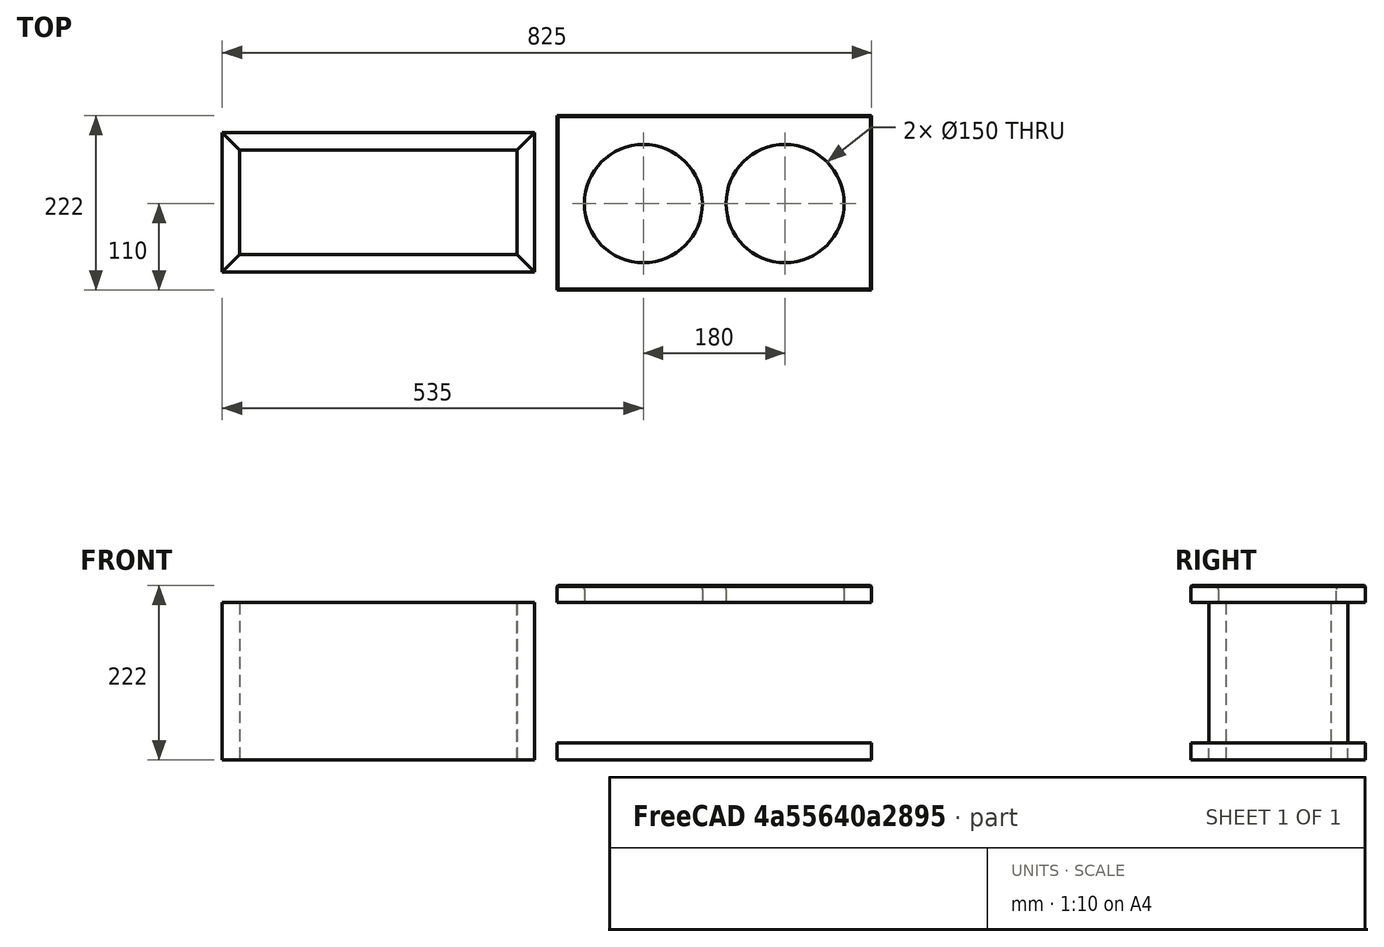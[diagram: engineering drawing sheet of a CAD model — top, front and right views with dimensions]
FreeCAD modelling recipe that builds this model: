
FCSTD DOCUMENT  (FreeCAD 0.16R6706 (Git))
Label: planter
License: All rights reserved
LicenseURL: http://en.wikipedia.org/wiki/All_rights_reserved
objects: Part::Box×14, Part::Cut×10, Part::Extrusion×2, Part::Fillet×2, Part::Part2DObjectPython×1, Part::Chamfer×1
note: 30 computed .brp shape members not serialized (recipe doc carries the construction recipe); baked Part::Feature solids carry a one-line shape summary decoded from their .brp

FEATURE [Part::Box] Box  label="front"
  Height = 200
  Length = 400
  Placement = pos=(-425,23,0) rot=(0,0,1;0rad)
  Width = 22
FEATURE [Part::Box] Box002  label="left"
  Height = 200
  Length = 178
  Placement = pos=(-400,22,0) rot=(0,0,1;1.5708rad)
  Width = 22
FEATURE [Part::Box] Box004  label="base"
  Height = 222
  Length = 400
  Placement = pos=(0,222,0) rot=(1,0,0;1.5708rad)
  Width = 22
FEATURE [Part::Box] Box005  label="top"
  Height = 222
  Length = 400
  Placement = pos=(0,222,200) rot=(1,0,0;1.5708rad)
  Width = 22
FEATURE [Part::Part2DObjectPython] Circle  # Draft 2D object (typed FeaturePython)
  FirstAngle = 0
  LastAngle = 0
  MakeFace = true
  Placement = pos=(110,110,222) rot=(0,0,1;1.5708rad)
  Radius = 75
FEATURE [Part::Extrusion] Extrude
  Base = -> Circle
  Dir = (0,0,22)
  Placement = pos=(0,0,-22) rot=(0,0,1;0rad)
  Solid = true
FEATURE [Part::Extrusion] Extrude001
  Base = -> Circle
  Dir = (0,0,22)
  Placement = pos=(180,0,-22) rot=(0,0,1;0rad)
  Solid = true
FEATURE [Part::Cut] Cut
  Base = -> Box005
  Tool = -> Extrude
FEATURE [Part::Cut] Cut001
  Base = -> Cut
  Tool = -> Extrude001
FEATURE [Part::Fillet] Fillet
  Base = -> Cut001
  Edges = 1 edges r=5: [Edge15]
FEATURE [Part::Chamfer] Chamfer
  Base = -> Fillet
  Edges = 4 edges r=1.5: [Edge2,Edge3,Edge4,Edge5]
FEATURE [Part::Fillet] Fillet001  label="Top"
  Base = -> Chamfer
  Edges = 1 edges r=5: [Edge6]
FEATURE [Part::Box] Box006  label="45degree"
  Height = 300
  Length = 24
  Placement = pos=(-26.4,21,-14) rot=(0,0,1;0.785398rad)
  Width = 36
FEATURE [Part::Box] Box007  label="45degree001"
  Height = 300
  Length = 23
  Placement = pos=(-443.5,37,-31) rot=(0,0,-1;0.785398rad)
  Width = 36
FEATURE [Part::Box] Box008  label="front001"
  Height = 200
  Length = 400
  Placement = pos=(25,0,0) rot=(0,0,1;0rad)
  Width = 22
FEATURE [Part::Box] Box009  label="45degree002"
  Height = 300
  Length = 23
  Placement = pos=(425,0,-16) rot=(0,0,1;0.785398rad)
  Width = 34
FEATURE [Part::Cut] Cut004
  Base = -> Box008
  Placement = pos=(0,-31,0) rot=(0,0,1;0rad)
  Tool = -> Box009
FEATURE [Part::Box] Box010  label="45degree003"
  Height = 300
  Length = 25
  Placement = pos=(9,-15,-33) rot=(0,0,-1;0.785398rad)
  Width = 35
FEATURE [Part::Cut] Cut005  label="Back"
  Base = -> Cut004
  Placement = pos=(0,169,0) rot=(0,0,1;3.14159rad)
  Tool = -> Box010
FEATURE [Part::Box] Box012  label="45degree004"
  Height = 300
  Length = 23
  Placement = pos=(-400,178,-33) rot=(0,0,1;0.785398rad)
  Width = 32
FEATURE [Part::Box] Box013  label="45degree005"
  Height = 300
  Length = 23
  Placement = pos=(-423,22,-31) rot=(0,0,-1;0.785398rad)
  Width = 33
FEATURE [Part::Cut] Cut006
  Base = -> Box002
  Tool = -> Box013
FEATURE [Part::Cut] Cut007  label="Left"
  Base = -> Cut006
  Placement = pos=(-3,0,0) rot=(0,0,1;0rad)
  Tool = -> Box012
FEATURE [Part::Box] Box014  label="left001"
  Height = 200
  Length = 178
  Placement = pos=(-400,22,0) rot=(0,0,1;1.5708rad)
  Width = 22
FEATURE [Part::Box] Box015  label="45degree006"
  Height = 300
  Length = 23
  Placement = pos=(-400,178,-33) rot=(0,0,1;0.785398rad)
  Width = 32
FEATURE [Part::Box] Box016  label="45degree007"
  Height = 300
  Length = 23
  Placement = pos=(-423,22,-31) rot=(0,0,-1;0.785398rad)
  Width = 33
FEATURE [Part::Cut] Cut008
  Base = -> Box014
  Tool = -> Box016
FEATURE [Part::Cut] Cut009  label="Right"
  Base = -> Cut008
  Placement = pos=(-450.34,223,0) rot=(0,0,1;3.14159rad)
  Tool = -> Box015
FEATURE [Part::Cut] Cut010
  Base = -> Box
  Tool = -> Box006
FEATURE [Part::Cut] Cut011
  Base = -> Cut010
  Tool = -> Box007
